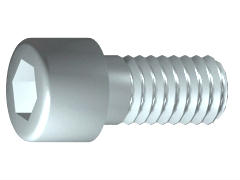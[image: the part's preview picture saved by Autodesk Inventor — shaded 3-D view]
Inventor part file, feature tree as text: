
AUTODESK INVENTOR PART (.ipt)
format: ipt  version: unknown  size: 288,256 bytes
history: native  units: mm (DEFAULTED — no unit token found)
features: extrude x1, plane x1, fillet x1
ambient origin geometry x7: Origin, YZ Plane, XY Plane, X Axis, Y Axis, Z Axis, Center Point
bodies: Solid1 (feature_tree), Body (feature_tree)
feature tree (3):
  extrude  "Slot"  Depth=24.209048mm
  plane  "Work Plane1"
  fillet  "Fillet2"  Radius=1.190852mm
